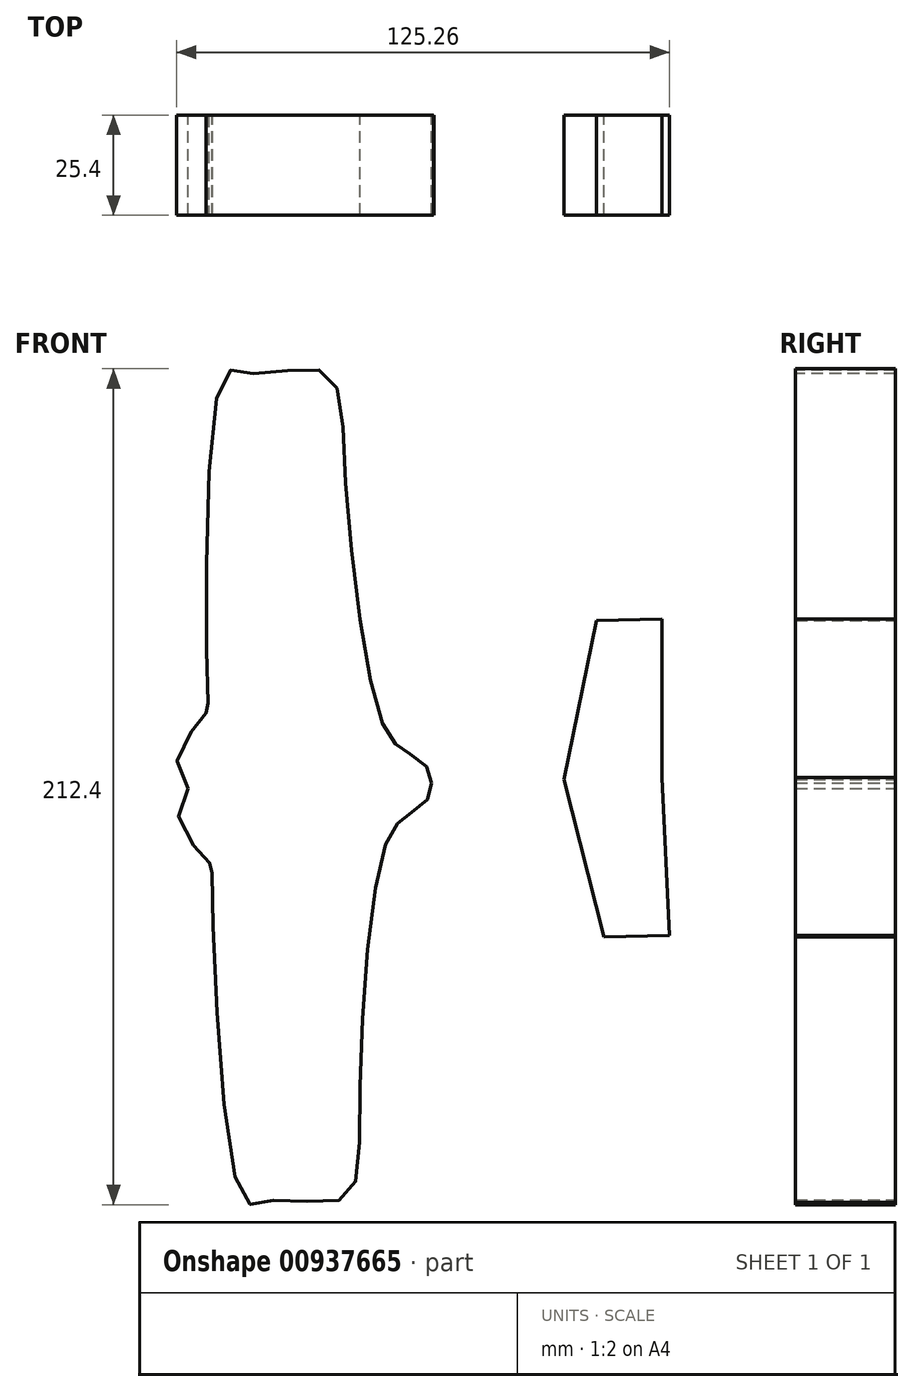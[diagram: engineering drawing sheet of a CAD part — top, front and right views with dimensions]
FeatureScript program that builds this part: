
annotation { "Feature Type Name" : "Feature", "Feature Type Description" : "" }
export const myFeature = defineFeature(function(context is Context, id is Id, definition is map)
    precondition{}
    {
        {
            var Q0;
            Q0=qCreatedBy(makeId("Front.planeOp"),FACE);
            var sketch = newSketch(context, id + "F0", { "sketchPlane" : qUnion([Q0])});
            skLineSegment(sketch, "E0.bottom", {"start": v(-27.2, 114.3) * mm, "end": v(74.4, 114.3) * mm, "construction": true});
            skLineSegment(sketch, "E0.top", {"start": v(-27.2, -114.3) * mm, "end": v(74.4, -114.3) * mm, "construction": true});
            skLineSegment(sketch, "E0.left", {"start": v(-27.2, 114.3) * mm, "end": v(-27.2, -114.3) * mm, "construction": true});
            skLineSegment(sketch, "E0.right", {"start": v(74.4, 114.3) * mm, "end": v(74.4, -114.3) * mm, "construction": true});
            skPoint(sketch, "E0.middle", {"position": v(23.6, 0) * mm});
            skLineSegment(sketch, "E1", {"start": v(-61.4, 0) * mm, "end": v(121.3, 4.34) * mm, "construction": true});
            skFitSpline(sketch, "E2", {"points": [v(-16.25, 1.07) * mm, v(-15.72, 15.24) * mm, v(-11.05, 20.95) * mm, v(-11.05, 21.47) * mm, v(-7.41, 105.55) * mm, v(0, 106.6) * mm, v(18.02, 107.1) * mm, v(23.6, 82.2) * mm, v(33.07, 17.83) * mm, v(38.26, 11.09) * mm, v(43.45, 7.45) * mm, v(45.55, 2.54) * mm, v(-16.25, 1.07) * mm]});
            skFitSpline(sketch, "E3.MirrorC", {"points": [v(-16.25, 1.07) * mm, v(-15.05, -13.05) * mm, v(-10.11, -18.53) * mm, v(-10.09, -19.05) * mm, v(-2.47, -102.87) * mm, v(4.99, -103.56) * mm, v(23.01, -103.22) * mm, v(27.4, -78.07) * mm, v(33.81, -13.33) * mm, v(38.68, -6.34) * mm, v(43.69, -2.47) * mm, v(45.55, 2.54) * mm, v(-16.25, 1.07) * mm]});
            skLineSegment(sketch, "E4", {"start": v(79.31, 3.34) * mm, "end": v(87.57, 43.79) * mm});
            skLineSegment(sketch, "E5", {"start": v(87.57, 43.79) * mm, "end": v(104.2, 44.18) * mm});
            skLineSegment(sketch, "E6", {"start": v(104.2, 44.18) * mm, "end": v(104.2, 3.93) * mm});
            skLineSegment(sketch, "E7", {"start": v(104.2, 3.93) * mm, "end": v(79.31, 3.34) * mm});
            skLineSegment(sketch, "E8.MirrorCS", {"start": v(79.31, 3.34) * mm, "end": v(89.48, -36.67) * mm});
            skLineSegment(sketch, "E9.MirrorCS", {"start": v(89.48, -36.67) * mm, "end": v(106.1, -36.27) * mm});
            skLineSegment(sketch, "E10.MirrorCS", {"start": v(106.1, -36.27) * mm, "end": v(104.2, 3.93) * mm});
            skSolve(sketch);
        }
        {
            var Q0;
            Q0 = qSketchRegion(id + "F0", true);
            extrude(context, id + "F1", {"entities" : qUnion([Q0]), "depth" : 25.4 * mm, "offsetDistance" : 25.4 * mm});
        }
    });
